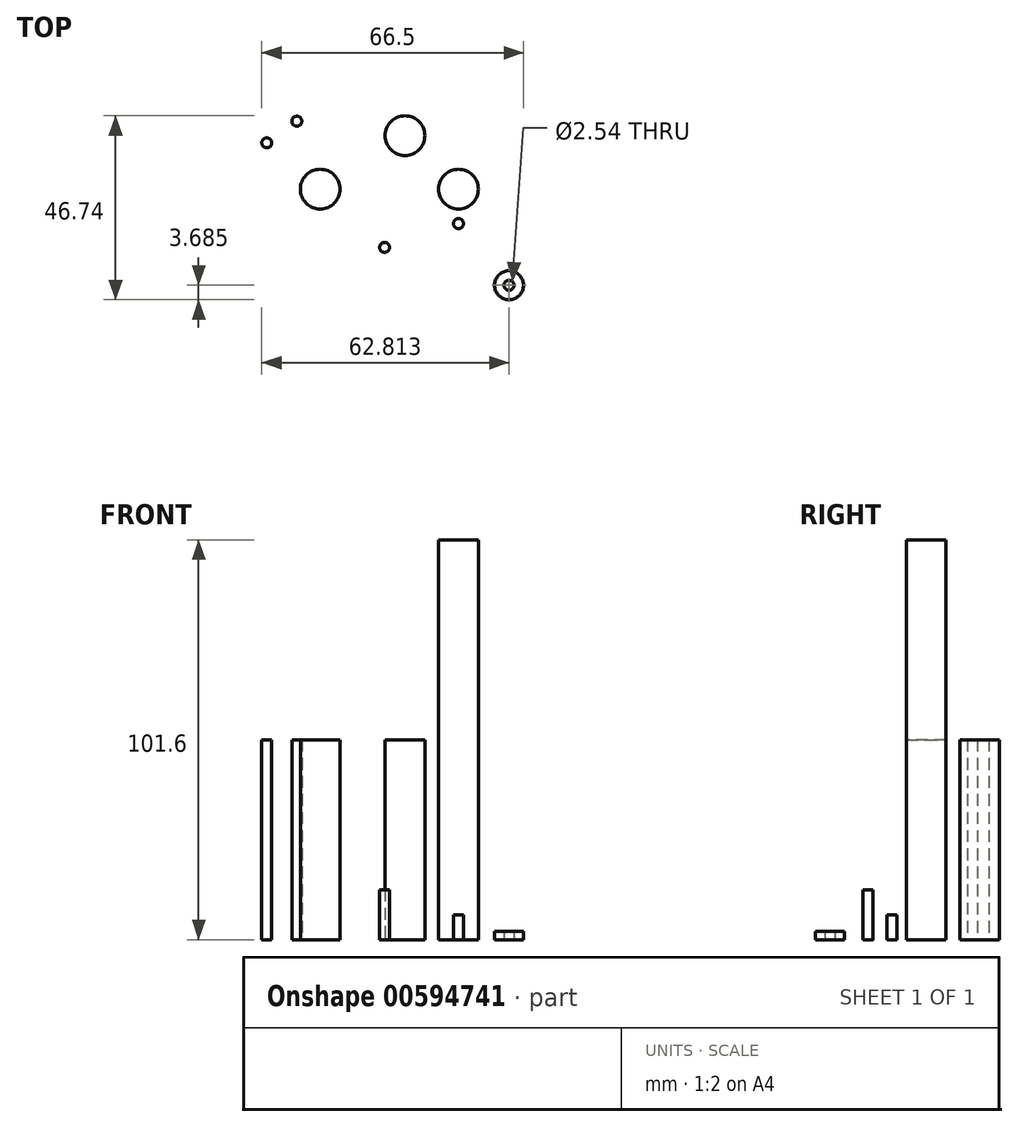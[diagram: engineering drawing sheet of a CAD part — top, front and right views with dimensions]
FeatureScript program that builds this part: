
annotation { "Feature Type Name" : "Feature", "Feature Type Description" : "" }
export const myFeature = defineFeature(function(context is Context, id is Id, definition is map)
    precondition{}
    {
        {
            var Q0;
            Q0=qCreatedBy(makeId("Top.planeOp"),FACE);
            var sketch = newSketch(context, id + "F0", { "sketchPlane" : qUnion([Q0])});
            skCircle(sketch, "E0", {"center": v(0, 0) * mm, "radius": 5.04 * mm});
            skSolve(sketch);
        }
        {
            var Q0;
            Q0=makeQuery(id+"F0.imprint","IMPRINT",FACE,{"disambiguationData":[TD([[makeQuery(id+"F0.imprint","IMPRINT",EDGE,{"derivedFrom":sQuery(id+"F0.wireOp",EDGE,"E0")}),1.0]])]});
            extrude(context, id + "F1", {"entities" : qUnion([Q0]), "depth" : 101.6 * mm, "offsetDistance" : 25.4 * mm});
        }
        {
            var Q0;
            Q0=qCreatedBy(makeId("Top.planeOp"),FACE);
            var sketch = newSketch(context, id + "F2", { "sketchPlane" : qUnion([Q0])});
            skCircle(sketch, "E1", {"center": v(-35.13, 0) * mm, "radius": 5.04 * mm});
            skCircle(sketch, "E2", {"center": v(-13.59, 13.59) * mm, "radius": 5.04 * mm});
            skCircle(sketch, "E3", {"center": v(-41.07, 17.25) * mm, "radius": 1.27 * mm});
            skCircle(sketch, "E4", {"center": v(-48.7, 11.76) * mm, "radius": 1.27 * mm});
            skSolve(sketch);
        }
        {
            var Q0;
            Q0=makeQuery(id+"F2.imprint","IMPRINT",FACE,{"disambiguationData":[TD([[makeQuery(id+"F2.imprint","IMPRINT",EDGE,{"derivedFrom":sQuery(id+"F2.wireOp",EDGE,"E1")}),1.0]])]});
            var Q1;
            Q1=makeQuery(id+"F2.imprint","IMPRINT",FACE,{"disambiguationData":[TD([[makeQuery(id+"F2.imprint","IMPRINT",EDGE,{"derivedFrom":sQuery(id+"F2.wireOp",EDGE,"E2")}),1.0]])]});
            var Q2;
            Q2=makeQuery(id+"F2.imprint","IMPRINT",FACE,{"disambiguationData":[TD([[makeQuery(id+"F2.imprint","IMPRINT",EDGE,{"derivedFrom":sQuery(id+"F2.wireOp",EDGE,"E3")}),1.0]])]});
            var Q3;
            Q3=makeQuery(id+"F2.imprint","IMPRINT",FACE,{"disambiguationData":[TD([[makeQuery(id+"F2.imprint","IMPRINT",EDGE,{"derivedFrom":sQuery(id+"F2.wireOp",EDGE,"E4")}),1.0]])]});
            extrude(context, id + "F3", {"entities" : qUnion([Q0, Q1, Q2, Q3]), "depth" : 50.8 * mm, "offsetDistance" : 25.4 * mm});
        }
        {
            var Q0;
            Q0=qCreatedBy(makeId("Top.planeOp"),FACE);
            var sketch = newSketch(context, id + "F4", { "sketchPlane" : qUnion([Q0])});
            skCircle(sketch, "E5", {"center": v(0, -8.76) * mm, "radius": 1.27 * mm});
            skSolve(sketch);
        }
        {
            var Q0;
            Q0=makeQuery(id+"F4.imprint","IMPRINT",FACE,{"disambiguationData":[TD([[makeQuery(id+"F4.imprint","IMPRINT",EDGE,{"derivedFrom":sQuery(id+"F4.wireOp",EDGE,"E5")}),1.0]])]});
            extrude(context, id + "F5", {"entities" : qUnion([Q0]), "depth" : 6.35 * mm, "offsetDistance" : 25.4 * mm});
        }
        {
            var Q0;
            Q0=qCreatedBy(makeId("Top.planeOp"),FACE);
            var sketch = newSketch(context, id + "F6", { "sketchPlane" : qUnion([Q0])});
            skCircle(sketch, "E6", {"center": v(12.83, -24.43) * mm, "radius": 3.68 * mm});
            skCircle(sketch, "E7", {"center": v(12.83, -24.43) * mm, "radius": 1.27 * mm});
            skSolve(sketch);
        }
        {
            var Q0;
            Q0=makeQuery(id+"F6.imprint","IMPRINT",FACE,{"disambiguationData":[TD([[makeQuery(id+"F6.imprint","IMPRINT",EDGE,{"derivedFrom":sQuery(id+"F6.wireOp",EDGE,"E6")}),1.0]])]});
            extrude(context, id + "F7", {"entities" : qUnion([Q0]), "depth" : 2.1 * mm, "offsetDistance" : 25.4 * mm});
        }
        {
            var Q0;
            Q0=qCreatedBy(makeId("Top.planeOp"),FACE);
            var sketch = newSketch(context, id + "F8", { "sketchPlane" : qUnion([Q0])});
            skCircle(sketch, "E8", {"center": v(-18.78, -14.81) * mm, "radius": 1.27 * mm});
            skSolve(sketch);
        }
        {
            var Q0;
            Q0=makeQuery(id+"F8.imprint","IMPRINT",FACE,{"disambiguationData":[TD([[makeQuery(id+"F8.imprint","IMPRINT",EDGE,{"derivedFrom":sQuery(id+"F8.wireOp",EDGE,"E8")}),1.0]])]});
            extrude(context, id + "F9", {"entities" : qUnion([Q0]), "depth" : 12.7 * mm, "offsetDistance" : 25.4 * mm});
        }
    });
